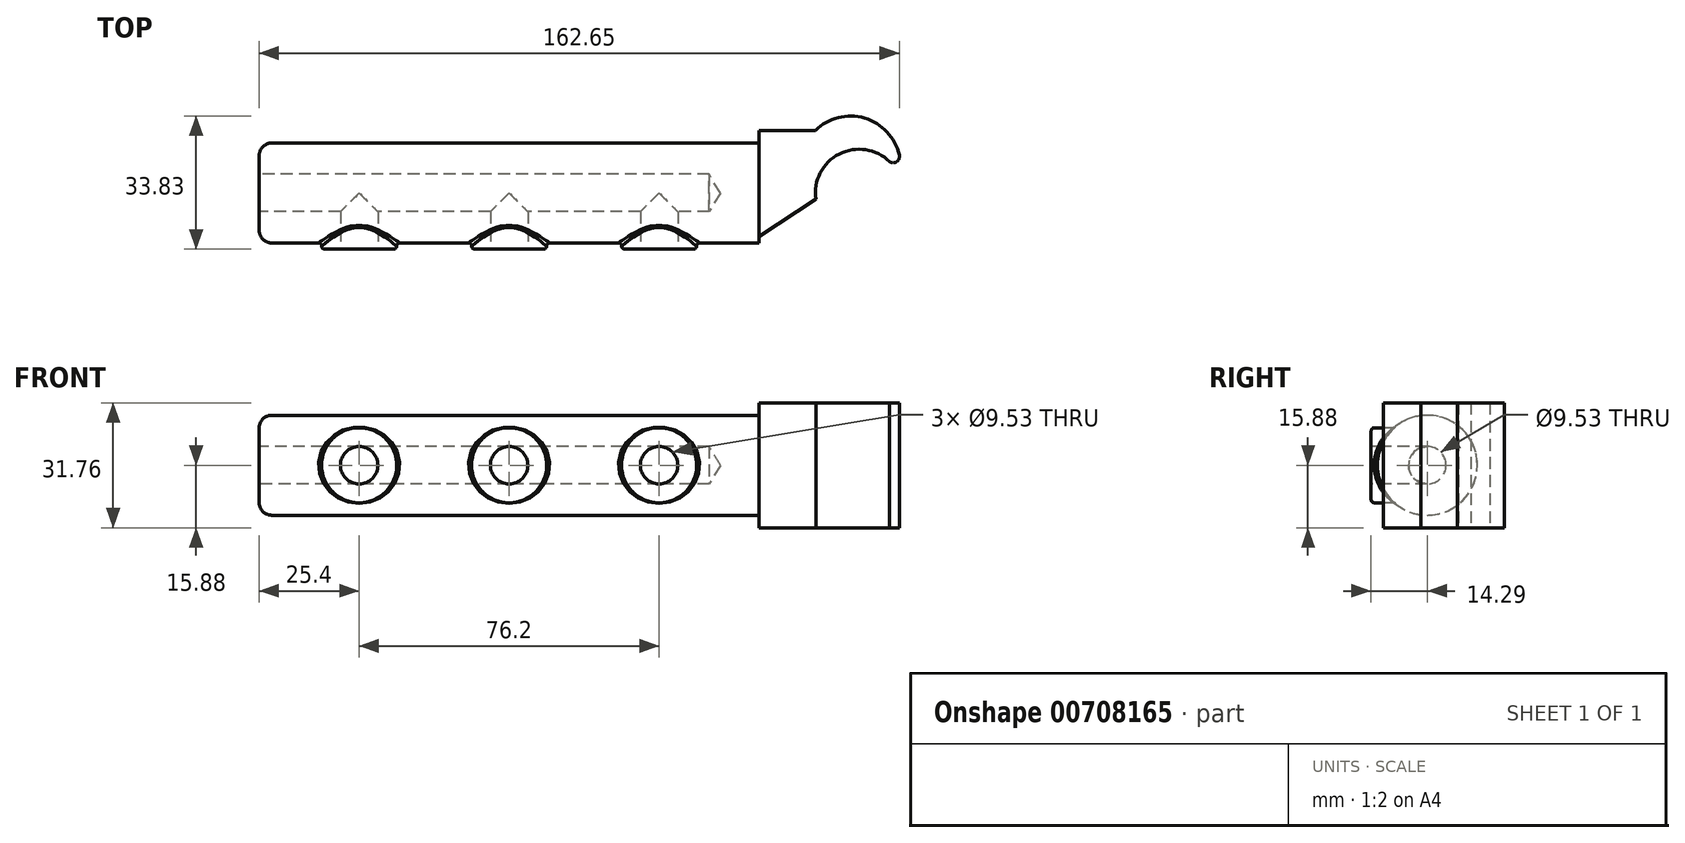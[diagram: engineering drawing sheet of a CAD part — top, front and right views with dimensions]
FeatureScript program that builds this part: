
annotation { "Feature Type Name" : "Feature", "Feature Type Description" : "" }
export const myFeature = defineFeature(function(context is Context, id is Id, definition is map)
    precondition{}
    {
        {
            var Q0;
            Q0=qCreatedBy(makeId("Top.planeOp"),FACE);
            var sketch = newSketch(context, id + "F0", { "sketchPlane" : qUnion([Q0])});
            skLineSegment(sketch, "E0", {"start": v(-25.4, 15.87) * mm, "end": v(-25.4, -11.11) * mm});
            skLineSegment(sketch, "E1", {"start": v(-25.4, 15.87) * mm, "end": v(-11.11, 15.87) * mm});
            skArc(sketch, "E2", {"start": v(10.22, 9.59) * mm, "mid": v(1.4, 19.03) * mm, "end": v(-11.11, 15.87) * mm});
            skArc(sketch, "E3", {"start": v(7.78, 7.94) * mm, "mid": v(9.55, 7.94) * mm, "end": v(10.22, 9.59) * mm});
            skLineSegment(sketch, "E4", {"start": v(-11, -1.59) * mm, "end": v(-25.4, -11.11) * mm});
            skPoint(sketch, "E5.visualSharp", {"position": v(-25.4, -11.11) * mm});
            skArc(sketch, "E6.trimOffspring", {"start": v(7.78, 7.94) * mm, "mid": v(-5.03, 9.91) * mm, "end": v(-11, -1.59) * mm});
            skSolve(sketch);
        }
        {
            var Q0;
            Q0 = qSketchRegion(id + "F0", true);
            extrude(context, id + "F1", {"entities" : qUnion([Q0]), "endBound" : BoundingType.SYMMETRIC, "depth" : 31.75 * mm, "offsetDistance" : 25.4 * mm});
        }
        {
            var Q0;
            Q0=makeQuery(id+"F1.opExtrude","SWEPT_FACE",FACE,{"disambiguationData":[OSD([sQuery(id+"F0.wireOp",EDGE,"E0")])]});
            var sketch = newSketch(context, id + "F2", { "sketchPlane" : qUnion([Q0])});
            skCircle(sketch, "E7", {"center": v(0, 0) * mm, "radius": 12.7 * mm});
            skSolve(sketch);
        }
        {
            var Q0;
            Q0 = qSketchRegion(id + "F2", true);
            extrude(context, id + "F3", {"entities" : qUnion([Q0]), "depth" : 127 * mm, "offsetDistance" : 25.4 * mm});
        }
        {
            var Q0;
            Q0=makeQuery(id+"F3.opExtrude","CAP_EDGE",EDGE,{"disambiguationData":[OSD([sQuery(id+"F2.wireOp",EDGE,"E7")])],"isStart":false});
            fillet(context, id + "F4", {"entities" : qUnion([Q0]), "radius" : 3.17 * mm, "tangentPropagation" : true, "allowEdgeOverflow" : false});
        }
        {
            var Q0;
            Q0=qCreatedBy(makeId("Front.planeOp"),FACE);
            cPlane(context, id + "F5", {"entities" : qUnion([Q0]), "cplaneType" : CPlaneType.OFFSET, "offset" : 14.29 * mm, "width" : 152.4 * mm, "height" : 152.4 * mm});
        }
        {
            var Q0;
            Q0=qCreatedBy(id+"F5.planeOp",FACE);
            var sketch = newSketch(context, id + "F6", { "sketchPlane" : qUnion([Q0])});
            skLineSegment(sketch, "E8", {"start": v(0, 0) * mm, "end": v(-160.18, 0) * mm, "construction": true});
            skLineSegment(sketch, "E9", {"start": v(-88.9, 36.45) * mm, "end": v(-88.9, -41.02) * mm, "construction": true});
            skCircle(sketch, "E10", {"center": v(-88.9, 0) * mm, "radius": 9.53 * mm});
            skCircle(sketch, "E11", {"center": v(-50.8, 0) * mm, "radius": 9.53 * mm});
            skCircle(sketch, "E12", {"center": v(-127, 0) * mm, "radius": 9.53 * mm});
            skSolve(sketch);
        }
        {
            var Q0;
            Q0 = qSketchRegion(id + "F6", true);
            extrude(context, id + "F7", {"entities" : qUnion([Q0]), "operationType" : NewBodyOperationType.ADD, "oppositeDirection" : true, "depth" : 12.7 * mm, "offsetDistance" : 25.4 * mm});
        }
        {
            var Q0;
            Q0=sQuery(id+"F6.wireOp",VERTEX,"E12.center");
            var Q1;
            Q1=sQuery(id+"F6.wireOp",VERTEX,"E10.center");
            var Q2;
            Q2=sQuery(id+"F6.wireOp",VERTEX,"E11.center");
            var Q3;
            Q3=makeQuery(id+"F3.opExtrude","SWEPT_BODY",BODY,{"disambiguationData":[OSD([sQuery(id+"F2.wireOp",EDGE,"E7")])]});
            hole(context, id + "F8", {"style" : HoleStyle.SIMPLE, "endStyle" : HoleEndStyle.BLIND, "holeDiameter" : 9.52 * mm, "majorDiameter" : 6.35 * mm, "holeDepth" : 14.29 * mm, "isTappedThrough" : true, "tappedDepth" : 12.7 * mm, "tapClearance" : 3, "startFromSketch" : true, "locations" : qUnion([Q0, Q1, Q2]), "scope" : qUnion([Q3])});
        }
        {
            var Q0;
            Q0=makeQuery(id+"F7.boolean.opBoolean","INTERSECT",EDGE,{"derivedFrom":[makeQuery(id+"F3.opExtrude","SWEPT_FACE",FACE,{"disambiguationData":[OSD([sQuery(id+"F2.wireOp",EDGE,"E7")])]}),makeQuery(id+"F7.opExtrude","SWEPT_FACE",FACE,{"disambiguationData":[OSD([sQuery(id+"F6.wireOp",EDGE,"E12")])]})]});
            var Q1;
            Q1=makeQuery(id+"F7.boolean.opBoolean","INTERSECT",EDGE,{"derivedFrom":[makeQuery(id+"F3.opExtrude","SWEPT_FACE",FACE,{"disambiguationData":[OSD([sQuery(id+"F2.wireOp",EDGE,"E7")])]}),makeQuery(id+"F7.opExtrude","SWEPT_FACE",FACE,{"disambiguationData":[OSD([sQuery(id+"F6.wireOp",EDGE,"E10")])]})]});
            var Q2;
            Q2=makeQuery(id+"F7.boolean.opBoolean","INTERSECT",EDGE,{"derivedFrom":[makeQuery(id+"F3.opExtrude","SWEPT_FACE",FACE,{"disambiguationData":[OSD([sQuery(id+"F2.wireOp",EDGE,"E7")])]}),makeQuery(id+"F7.opExtrude","SWEPT_FACE",FACE,{"disambiguationData":[OSD([sQuery(id+"F6.wireOp",EDGE,"E11")])]})]});
            fillet(context, id + "F9", {"entities" : qUnion([Q0, Q1, Q2]), "radius" : 0.8 * mm, "tangentPropagation" : true, "allowEdgeOverflow" : false});
        }
        {
            var Q0;
            Q0=makeQuery(id+"F7.opExtrude","CAP_EDGE",EDGE,{"disambiguationData":[OSD([sQuery(id+"F6.wireOp",EDGE,"E12")])],"isStart":true});
            var Q1;
            Q1=makeQuery(id+"F7.opExtrude","CAP_EDGE",EDGE,{"disambiguationData":[OSD([sQuery(id+"F6.wireOp",EDGE,"E10")])],"isStart":true});
            var Q2;
            Q2=makeQuery(id+"F7.opExtrude","CAP_EDGE",EDGE,{"disambiguationData":[OSD([sQuery(id+"F6.wireOp",EDGE,"E11")])],"isStart":true});
            fillet(context, id + "F10", {"entities" : qUnion([Q0, Q1, Q2]), "radius" : 0.8 * mm, "tangentPropagation" : true, "allowEdgeOverflow" : false});
        }
        {
            var Q0;
            Q0=makeQuery(id+"F3.opExtrude","CAP_FACE",FACE,{"disambiguationData":[OSD([sQuery(id+"F2.wireOp",EDGE,"E7")])],"isStart":false});
            var sketch = newSketch(context, id + "F11", { "sketchPlane" : qUnion([Q0])});
            skCircle(sketch, "E13", {"center": v(0, 0) * mm, "radius": 4.76 * mm});
            skSolve(sketch);
        }
        {
            var Q0;
            Q0=sQuery(id+"F11.wireOp",VERTEX,"E13.center");
            var Q1;
            Q1=makeQuery(id+"F3.opExtrude","SWEPT_BODY",BODY,{"disambiguationData":[OSD([sQuery(id+"F2.wireOp",EDGE,"E7")])]});
            hole(context, id + "F12", {"style" : HoleStyle.SIMPLE, "endStyle" : HoleEndStyle.BLIND, "holeDiameter" : 9.52 * mm, "majorDiameter" : 6.35 * mm, "holeDepth" : 114.3 * mm, "isTappedThrough" : true, "tappedDepth" : 12.7 * mm, "tapClearance" : 3, "startFromSketch" : true, "locations" : qUnion([Q0]), "scope" : qUnion([Q1])});
        }
    });
